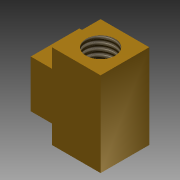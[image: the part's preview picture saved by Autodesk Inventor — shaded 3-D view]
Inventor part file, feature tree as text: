
AUTODESK INVENTOR PART (.ipt)
format: ipt  version: 2011 (Build 150239000, 239)  size: 112,128 bytes
history: native  units: mm (DEFAULTED — no unit token found)
features: extrude x4, sketch x4, thread x3, projected_geometry x3
ambient origin geometry x8: Origin, YZ Plane, XZ Plane, XY Plane, X Axis, Y Axis, Z Axis, Center Point
bodies: Solid1 (feature_tree)
feature tree (14):
  extrude  "Extrusion1"  Depth=14.605mm
  extrude  "Extrusion2"  Depth=14.224mm
  extrude  "Extrusion3"  Depth=8.763mm
  extrude  "Extrusion4"  Depth=8.763mm
  thread  "Thread1"  [1 undecoded]
  thread  "Thread2"  [1 undecoded]
  thread  "Thread3"  [1 undecoded]
  sketch  "Sketch1"  dims[d0=14.605mm d1=14.605mm]
  sketch  "Sketch2"  dims[d2=25.4mm d3=0.0mm d4=14.224mm]
  projected_geometry  "Projected Loop1"
  sketch  "Sketch3"  dims[d5=6.35mm d6=0.0mm d7=8.763mm]
  projected_geometry  "Projected Loop2"
  sketch  "Sketch4"  dims[d8=6.35mm d9=0.0mm d10=8.763mm d11=13.7414mm d12=0.0mm d13=8.89mm d14=0.0mm d15=8.89mm d16=0.0mm d17=8.89mm d18=0.0mm]
  projected_geometry  "Projected Loop3"
note: 3 required parameter values undecoded (feature->parameter linkage not recoverable at this tier; creation-order binding heuristic only, values carry confidence <= 0.55)
